# Revit family: Faucet-DXV-Percy-D351054XX_Series
name_source: partatom
category: Plumbing Fixtures
revit_build: Autodesk Revit 2014 (Build: 20130308_1515(x64)
units: mm (PartAtom-declared; Revit-internal decimal feet)

## types (10) — shared parameters
Assembly Code = D2020300
CW Connection = Yes
CWFU = 1.5
Cold Water Connection Diameter = 1/2"
Default Elevation = 38"
Description = Percy Wall Mount Faucet
HW Connection = Yes
HWFU = 1.5
Height = 2 5/16"
Hot Water Connection Diameter = 1"
Installation Type = Wall Mounted
Length = 7 5/8"
Manufacturer = DXV
Price = Prices may vary. Please consult Manufacturer Representative for most up-to-date price list.
Product Page URL = https://www.dxv.com
Revised Date = 05/07/2018
URL = www.dxv.com
Vent Connection = No
WFU = 2
Warranty Documentation Link = https://www.dxv.com
Waste Connection = No
Width = 12 9/32"

## per-type parameters (varying)
| type | ADA Compliant | Cross Handle Option | Finish | Flow Rate | Lever Handle Option | Material | Tri-Spoke Handle Option |
| D35105450.144 | Yes | No | Metal-DXV-144-Brushed Nickel | 1.5 GPM (5.7L/min) | Yes | Metal-DXV-144-Brushed Nickel | No |
| D35105450.100 | Yes | No | Metal-DXV-100-Polished Chrome | 1.5 GPM (5.7L/min) | Yes | Metal-DXV-100-Polished Chrome | No |
| D35105454.100 | No | Yes | Metal-DXV-100-Polished Chrome | 1.5 GPM (5.7L/min) | No | Metal-DXV-100-Polished Chrome | No |
| D35105454.144 | No | Yes | Metal-DXV-144-Brushed Nickel | 1.5 GPM (5.7L/min) | No | Metal-DXV-144-Brushed Nickel | No |
| D3510545C.100 | Yes | No | Metal-DXV-100-Polished Chrome | 1.2 GPM (4.5L/min) | Yes | Metal-DXV-100-Polished Chrome | No |
| D3510545C.144 | Yes | No | Metal-DXV-144-Brushed Nickel | 1.2 GPM (4.5L/min) | Yes | Metal-DXV-144-Brushed Nickel | No |
| D3510546C.100 | No | Yes | Metal-DXV-100-Polished Chrome | 1.2 GPM (4.5L/min) | No | Metal-DXV-100-Polished Chrome | No |
| D3510546C.144 | No | Yes | Metal-DXV-144-Brushed Nickel | 1.2 GPM (4.5L/min) | No | Metal-DXV-144-Brushed Nickel | No |
| D35105470.100 | Yes | No | Metal-DXV-100-Polished Chrome | 1.2 GPM (4.5L/min) | No | Metal-DXV-100-Polished Chrome | Yes |
| D35105470.144 | Yes | No | Metal-DXV-144-Brushed Nickel | 1.2 GPM (4.5L/min) | No | Metal-DXV-144-Brushed Nickel | Yes |

note: column(s) folded — value = type name in every type: Model

## geometry (parser evidence)
native form markers: Sweep x1
no freeform markers — native parametric forms only
